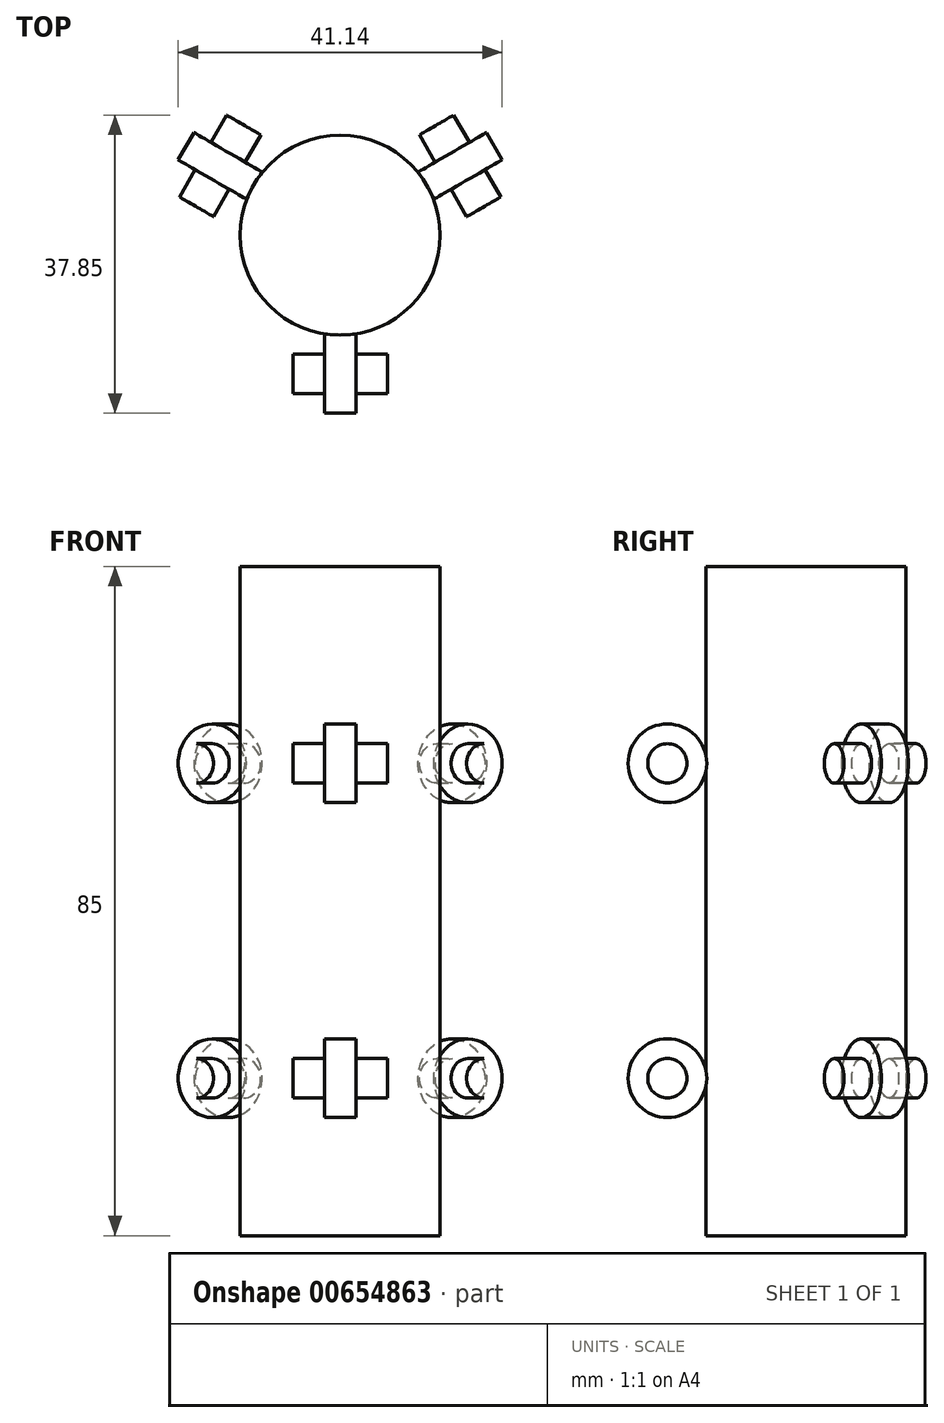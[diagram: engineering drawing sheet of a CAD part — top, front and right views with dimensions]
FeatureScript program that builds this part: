
annotation { "Feature Type Name" : "Feature", "Feature Type Description" : "" }
export const myFeature = defineFeature(function(context is Context, id is Id, definition is map)
    precondition{}
    {
        {
            var Q0;
            Q0=qCreatedBy(makeId("Right.planeOp"),FACE);
            var sketch = newSketch(context, id + "F0", { "sketchPlane" : qUnion([Q0])});
            skCircle(sketch, "E0", {"center": v(0, 0) * mm, "radius": 2.5 * mm});
            skCircle(sketch, "E1", {"center": v(0, 0) * mm, "radius": 5 * mm});
            skSolve(sketch);
        }
        {
            var Q0;
            Q0=makeQuery(id+"F0.imprint","IMPRINT",FACE,{"disambiguationData":[TD([[makeQuery(id+"F0.imprint","IMPRINT",EDGE,{"derivedFrom":sQuery(id+"F0.wireOp",EDGE,"E0")}),-1.0]])]});
            extrude(context, id + "F1", {"entities" : qUnion([Q0]), "endBound" : BoundingType.SYMMETRIC, "depth" : 4 * mm, "offsetDistance" : 25 * mm});
        }
        {
            var Q0;
            Q0=makeQuery(id+"F0.imprint","IMPRINT",FACE,{"disambiguationData":[TD([[makeQuery(id+"F0.imprint","IMPRINT",EDGE,{"derivedFrom":sQuery(id+"F0.wireOp",EDGE,"E0")}),1.0]])]});
            extrude(context, id + "F2", {"entities" : qUnion([Q0]), "operationType" : NewBodyOperationType.ADD, "endBound" : BoundingType.SYMMETRIC, "depth" : 12 * mm, "offsetDistance" : 25 * mm});
        }
        {
            var Q0;
            Q0=qCreatedBy(makeId("Top.planeOp"),FACE);
            var sketch = newSketch(context, id + "F3", { "sketchPlane" : qUnion([Q0])});
            skCircle(sketch, "E2", {"center": v(0, 0) * mm, "radius": 12.7 * mm});
            skSolve(sketch);
        }
        {
            var Q0;
            Q0=makeQuery(id+"F1.opExtrude","SWEPT_BODY",BODY,{"disambiguationData":[OSD([sQuery(id+"F0.wireOp",EDGE,"E0"),sQuery(id+"F0.wireOp",EDGE,"E1")])]});
            transform(context, id + "F4", {"entities" : qUnion([Q0]), "transformType" : TransformType.TRANSLATION_3D, "dx" : 0 * mm, "dy" : -17.6 * mm, "dz" : 0 * mm, "makeCopy" : false});
        }
        {
            var Q0;
            Q0=makeQuery(id+"F1.opExtrude","SWEPT_BODY",BODY,{"disambiguationData":[OSD([sQuery(id+"F0.wireOp",EDGE,"E0"),sQuery(id+"F0.wireOp",EDGE,"E1")])]});
            var Q1;
            Q1=sQuery(id+"F3.wireOp",EDGE,"E2");
            circularPattern(context, id + "F5", {"entities" : qUnion([Q0]), "axis" : qUnion([Q1]), "angle" : 360 * degree, "instanceCount" : 3, "equalSpace" : true});
        }
        {
            var Q0;
            Q0=makeQuery(id+"F1.opExtrude","SWEPT_BODY",BODY,{"disambiguationData":[OSD([sQuery(id+"F0.wireOp",EDGE,"E0"),sQuery(id+"F0.wireOp",EDGE,"E1")])]});
            var Q1;
            Q1=makeQuery(id+"F5.opPattern","COPY",BODY,{"derivedFrom":makeQuery(id+"F1.opExtrude","SWEPT_BODY",BODY,{"disambiguationData":[OSD([sQuery(id+"F0.wireOp",EDGE,"E0"),sQuery(id+"F0.wireOp",EDGE,"E1")])]}),"instanceName":"1"});
            var Q2;
            Q2=makeQuery(id+"F5.opPattern","COPY",BODY,{"derivedFrom":makeQuery(id+"F1.opExtrude","SWEPT_BODY",BODY,{"disambiguationData":[OSD([sQuery(id+"F0.wireOp",EDGE,"E0"),sQuery(id+"F0.wireOp",EDGE,"E1")])]}),"instanceName":"2"});
            transform(context, id + "F6", {"entities" : qUnion([Q0, Q1, Q2]), "transformType" : TransformType.TRANSLATION_3D, "dx" : 0 * mm, "dy" : 0 * mm, "dz" : -40 * mm, "makeCopy" : true});
        }
        {
            var Q0;
            Q0 = qSketchRegion(id + "F3", true);
            extrude(context, id + "F7", {"entities" : qUnion([Q0]), "depth" : 25 * mm, "offsetDistance" : 25 * mm, "hasSecondDirection" : true, "secondDirectionOppositeDirection" : true, "secondDirectionDepth" : 60 * mm});
        }
    });
